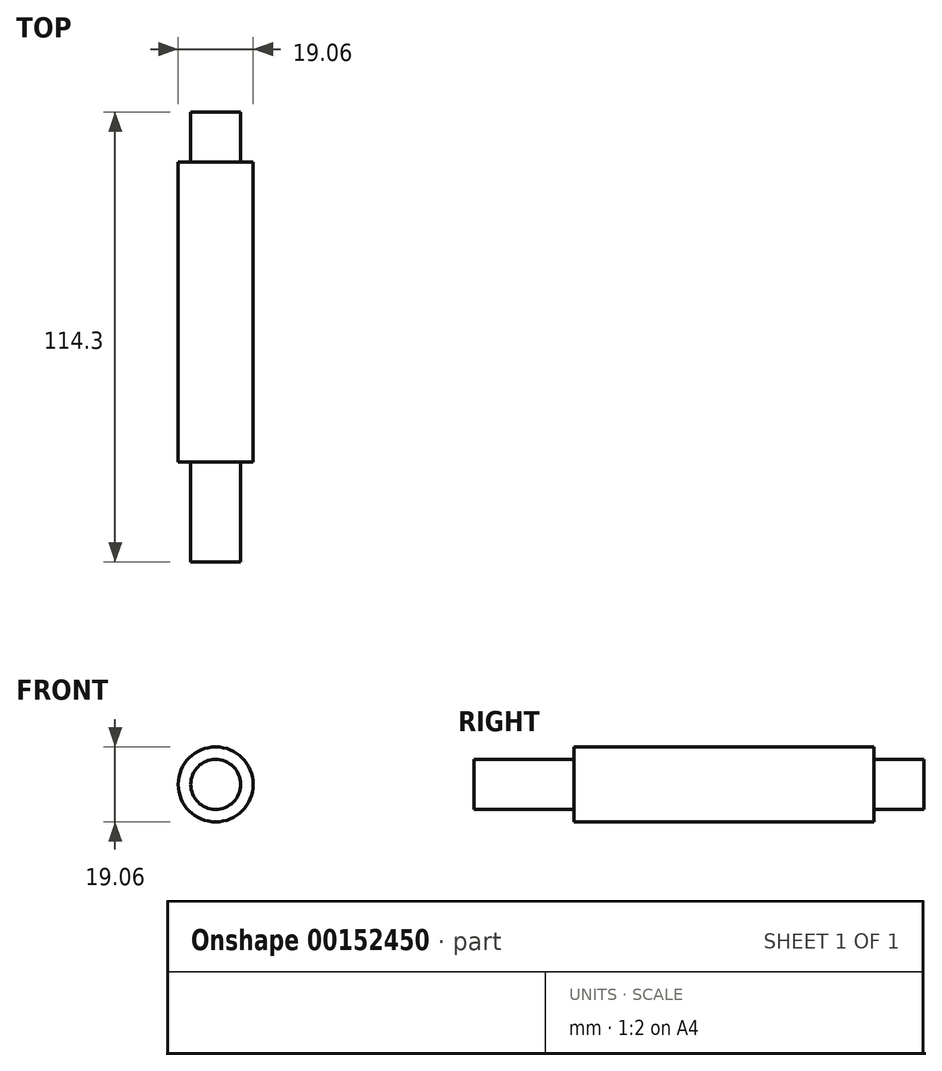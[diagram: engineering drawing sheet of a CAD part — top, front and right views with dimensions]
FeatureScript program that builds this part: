
annotation { "Feature Type Name" : "Feature", "Feature Type Description" : "" }
export const myFeature = defineFeature(function(context is Context, id is Id, definition is map)
    precondition{}
    {
        {
            var Q0;
            Q0=qCreatedBy(makeId("Front.planeOp"),FACE);
            var sketch = newSketch(context, id + "F0", { "sketchPlane" : qUnion([Q0])});
            skCircle(sketch, "E0", {"center": v(0, 0) * mm, "radius": 6.35 * mm});
            skSolve(sketch);
        }
        {
            var Q0;
            Q0=qSketchRegion(id+"F0",true);
            var Q1;
            Q1 = qSketchRegion(id + "F4", true);
            extrude(context, id + "F1", {"entities" : qUnion([Q0, Q1]), "depth" : 25.4 * mm});
        }
        {
            var Q0;
            Q0=qCreatedBy(makeId("Front.planeOp"),FACE);
            var sketch = newSketch(context, id + "F2", { "sketchPlane" : qUnion([Q0])});
            skCircle(sketch, "E1", {"center": v(0, 0) * mm, "radius": 9.53 * mm});
            skSolve(sketch);
        }
        {
            var Q0;
            Q0=qSketchRegion(id+"F2",true);
            extrude(context, id + "F3", {"entities" : qUnion([Q0]), "operationType" : NewBodyOperationType.ADD, "oppositeDirection" : true, "depth" : 76.2 * mm});
        }
        {
            var Q0;
            Q0=makeQuery(id+"F3.opExtrude","CAP_FACE",FACE,{"disambiguationData":[OSD([sQuery(id+"F2.wireOp",EDGE,"E1")])],"isStart":false});
            var sketch = newSketch(context, id + "F4", { "sketchPlane" : qUnion([Q0])});
            skCircle(sketch, "E2", {"center": v(0, 0) * mm, "radius": 6.35 * mm});
            skSolve(sketch);
        }
        {
            var Q0;
            Q0=qSketchRegion(id+"F4",true);
            extrude(context, id + "F5", {"entities" : qUnion([Q0]), "operationType" : NewBodyOperationType.ADD, "depth" : 12.7 * mm});
        }
    });
